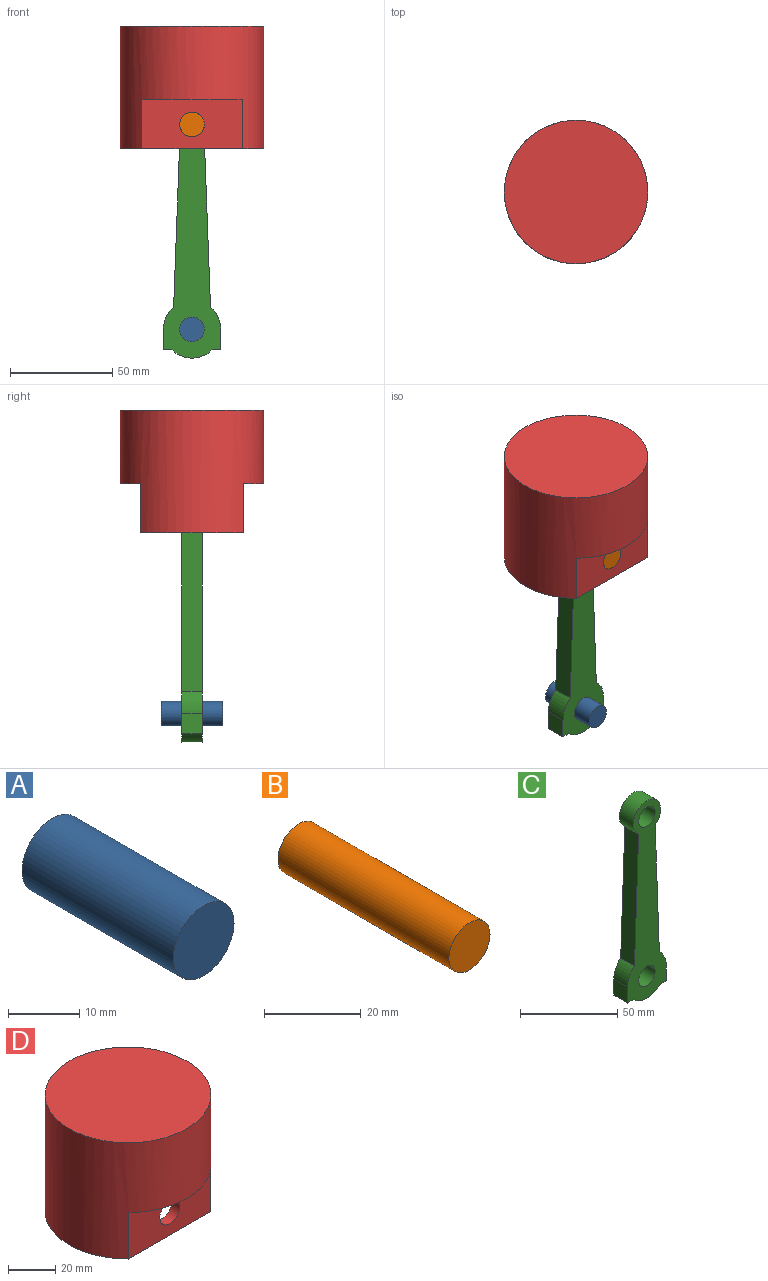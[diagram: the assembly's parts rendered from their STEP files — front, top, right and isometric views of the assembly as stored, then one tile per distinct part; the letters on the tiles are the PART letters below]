
ASSEMBLY  parts=4 mates=3
PART A: 3 faces, bbox 12x30x12 mm
  f0: cylinder r=6mm len=30mm, axis (0,1,0), area 1131mm2, adj f1,f2
  f1: plane 12x12mm, normal (0,-1,0), area 113.1mm2, adj f0
  f2: plane 12x12mm, normal (0,1,0), area 113.1mm2, adj f0
PART B: 3 faces, bbox 12x50x12 mm
  f0: cylinder r=6mm len=50mm, axis (0,1,0), area 1885mm2, adj f1,f2
  f1: plane 12x12mm, normal (0,-1,0), area 113.1mm2, adj f0
  f2: plane 12x12mm, normal (0,1,0), area 113.1mm2, adj f0
PART C: 14 faces, bbox 28x10x124 mm
  f0: plane 81.28x10mm, normal (1,0,0.04), area 813.3mm2, adj f1,f10,f12,f13
  f1: cylinder r=10mm len=20mm, axis (0,1,0), area 499.6mm2, adj f0,f2,f12,f13
  f2: plane 81.28x10mm, normal (-1,0,0.04), area 813.3mm2, adj f1,f3,f12,f13
  f3: cylinder r=14mm len=10.72mm, axis (0,1,0), area 122.2mm2, adj f2,f4,f12,f13
  f4: plane 10x10mm, normal (-1,0,0), area 100mm2, adj f3,f5,f12,f13
  f5: plane 10x4.2mm, normal (0,0,-1), area 42mm2, adj f4,f6,f12,f13
  f6: cylinder r=14mm len=19.6mm, axis (0,1,0), area 217.1mm2, adj f5,f7,f12,f13
  f7: plane 10x4.2mm, normal (0,0,-1), area 42mm2, adj f6,f8,f12,f13
  f8: plane 10x10mm, normal (1,0,0), area 100mm2, adj f7,f10,f12,f13
  f9: cylinder r=6mm len=12mm, axis (0,1,0), area 377mm2, adj f12,f13
  f10: cylinder r=14mm len=10.72mm, axis (0,1,0), area 122.2mm2, adj f0,f8,f12,f13
  f11: cylinder r=6mm len=12mm, axis (0,1,0), area 377mm2, adj f12,f13
  f12: plane 124x28mm, normal (0,-1,0), area 1892.3mm2, adj f0,f1,f2,f3,f4,f5,f6,f7
  f13: plane 124x28mm, normal (0,1,0), area 1892.3mm2, adj f0,f1,f2,f3,f4,f5,f6,f7
PART D: 14 faces, bbox 70x70x60 mm
  f0: plane 70x50mm, normal (0,0,-1), area 966mm2, adj f1,f3,f6,f7,f8,f9,f10
  f1: cylinder r=35mm len=70mm, axis (0,0,-1), area 10590mm2, adj f0,f2,f3,f4,f5,f6
  f2: plane 70x70mm, normal (0,0,1), area 3848.5mm2, adj f1
  f3: plane 48.99x24mm, normal (0,-1,0), area 1062.7mm2, adj f0,f1,f4,f13
  f4: plane 48.99x10mm, normal (0,0,-1), area 337.2mm2, adj f1,f3
  f5: plane 48.99x10mm, normal (0,0,-1), area 337.2mm2, adj f1,f6
  f6: plane 48.99x24mm, normal (0,1,0), area 1062.7mm2, adj f0,f1,f5,f12
  f7: plane 44.72x24mm, normal (0,1,0), area 960.2mm2, adj f0,f8,f10,f11,f13
  f8: cylinder r=30mm len=40mm, axis (0,0,-1), area 1050.8mm2, adj f0,f7,f9,f11
  f9: plane 44.72x24mm, normal (0,-1,0), area 960.2mm2, adj f0,f8,f10,f11,f12
  f10: cylinder r=30mm len=40mm, axis (0,0,-1), area 1050.8mm2, adj f0,f7,f9,f11
  f11: plane 60x40mm, normal (0,0,-1), area 2207.9mm2, adj f7,f8,f9,f10
  f12: cylinder r=6mm len=12mm, axis (0,-1,0), area 188.5mm2, adj f6,f9
  f13: cylinder r=6mm len=12mm, axis (0,-1,0), area 188.5mm2, adj f3,f7
PLACE A t=(150.23,90.97,15.46)mm
PLACE B t=(150.23,90.97,15.46)mm
PLACE C t=(150.23,90.97,15.46)mm
PLACE D t=(150.23,90.97,15.46)mm
MATE revolute D.f12 <-> B.f0  axis (0,-1,0) through (150.23,65.97,177.46)mm
MATE fastened B.f0 <-> C.f1  axis (0,1,0) through (150.23,90.97,177.46)mm
MATE revolute A.f0 <-> C.f3  axis (0,1,0) through (150.23,90.97,77.46)mm
